# Revit family: Legrand_Atlantic_versione_orizzontale_riferimenti_036911_a_036981
name_source: partatom
category: Installations électriques
revit_build: Autodesk Revit 2018 (Build: 20170223_1515(x64)
units: mm (PartAtom-declared; Revit-internal decimal feet)

## family parameters
Basée sur le plan de construction = Non
Conserver l'orientation des annotations = Non
Cote de connecteur circulaire = Utiliser le diamètre
Couper avec des vides une fois chargée = Non
Numéro OmniClass = 23.80.00.00
Partagée = Non
Point de calcul de pièce = Non
Titre OmniClass = Electric Power and Lighting
Toujours verticalement = Oui
Type d'élément = Normal

## types (8) — shared parameters
Condizioni Generali di Utilizzo = https://export.legrand.com
ETIM Class = EC000058
Fabricant = Legrand
IK = 10
RAL = 7035
URL = www.legrand.fr
materiale = metallo
portello di vettro = Non
versione orizzontale = Oui
versione quadrata = Non
versione verticale = Non

## per-type parameters (varying)
| type | IP | Scatola 036911 | Scatola 036975 | Scatola 036976 | Scatola 036977 | Scatola 036978 | Scatola 036979 | Scatola 036980 | Scatola 036981 | altezza | lunghezza | numero di porte | peso | profondità |
| Legrand Atlantic 036911 | 66 | Oui | Non | Non | Non | Non | Non | Non | Non | 300 mm | 400 mm  [stored 1.31234 ft] | 1 | 6.20 kg | 160 mm  [stored 0.524934 ft] |
| Legrand Atlantic 036976 | 66 | Non | Non | Oui | Non | Non | Non | Non | Non | 400 mm  [stored 1.31234 ft] | 600 mm | 1 | 14.80 kg | 200 mm  [stored 0.656168 ft] |
| Legrand Atlantic 036975 | 66 | Non | Oui | Non | Non | Non | Non | Non | Non | 300 mm | 400 mm  [stored 1.31234 ft] | 1 | 14.10 kg | 200 mm  [stored 0.656168 ft] |
| Legrand Atlantic 036977 | 66 | Non | Non | Non | Oui | Non | Non | Non | Non | 400 mm  [stored 1.31234 ft] | 600 mm | 1 | 13.30 kg | 250 mm  [stored 0.82021 ft] |
| Legrand Atlantic 036978 | 55 | Non | Non | Non | Non | Oui | Non | Non | Non | 600 mm | 800 mm  [stored 2.62467 ft] | 2 | 32.60 kg | 300 mm |
| Legrand Atlantic 036979 | 55 | Non | Non | Non | Non | Non | Oui | Non | Non | 600 mm | 1000 mm  [stored 3.28084 ft] | 2 | 32.60 kg | 300 mm |
| Legrand Atlantic 036980 | 55 | Non | Non | Non | Non | Non | Non | Oui | Non | 800 mm  [stored 2.62467 ft] | 1000 mm  [stored 3.28084 ft] | 2 | 53.60 kg | 300 mm |
| Legrand Atlantic 036981 | 55 | Non | Non | Non | Non | Non | Non | Non | Oui | 1000 mm  [stored 3.28084 ft] | 1200 mm | 2 | 80.60 kg | 300 mm |

note: column(s) folded — value = type name in every type: Description

note: [stored X ft] marks values corroborated as IEEE doubles in the binary element streams (Revit-internal decimal feet)
